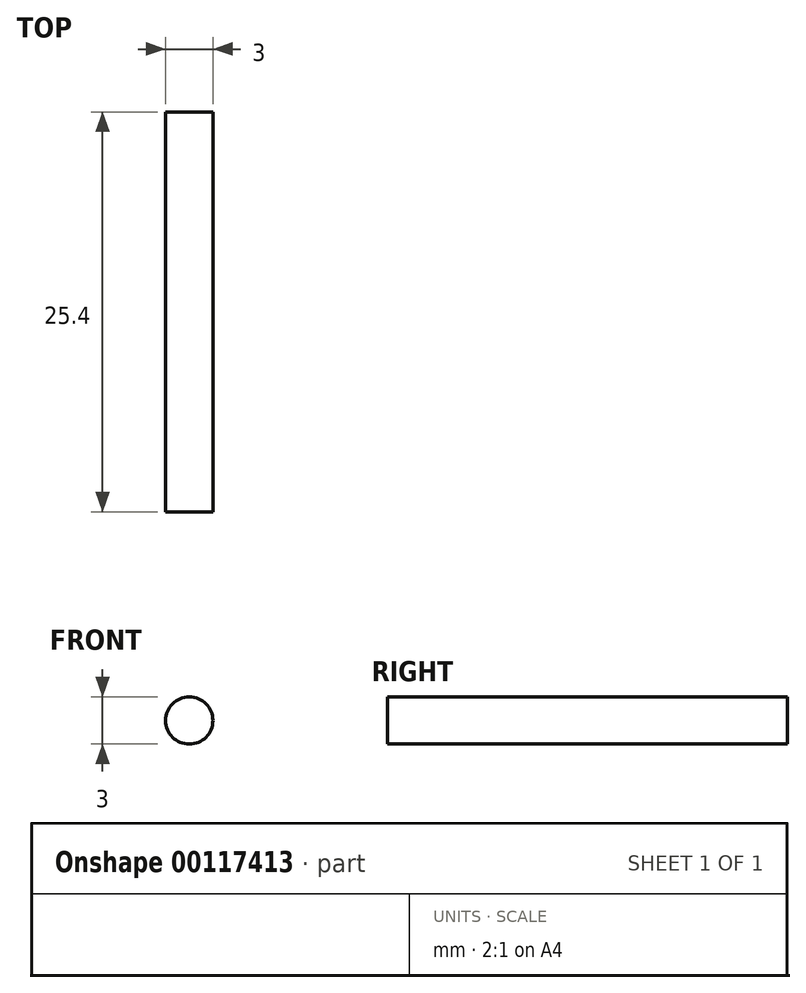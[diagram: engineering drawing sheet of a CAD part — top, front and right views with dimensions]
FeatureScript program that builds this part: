
annotation { "Feature Type Name" : "Feature", "Feature Type Description" : "" }
export const myFeature = defineFeature(function(context is Context, id is Id, definition is map)
    precondition{}
    {
        {
            var Q0;
            Q0=qCreatedBy(makeId("Front.planeOp"),FACE);
            var sketch = newSketch(context, id + "F0", { "sketchPlane" : qUnion([Q0])});
            skCircle(sketch, "E0", {"center": v(18.68, 12.5) * mm, "radius": 1.5 * mm});
            skSolve(sketch);
        }
        {
            var Q0;
            Q0=makeQuery(id+"F0.imprint","IMPRINT",FACE,{"disambiguationData":[TD([[makeQuery(id+"F0.imprint","IMPRINT",EDGE,{"derivedFrom":sQuery(id+"F0.wireOp",EDGE,"E0")}),1.0]])]});
            extrude(context, id + "F1", {"entities" : qUnion([Q0]), "depth" : 25.4 * mm});
        }
    });
